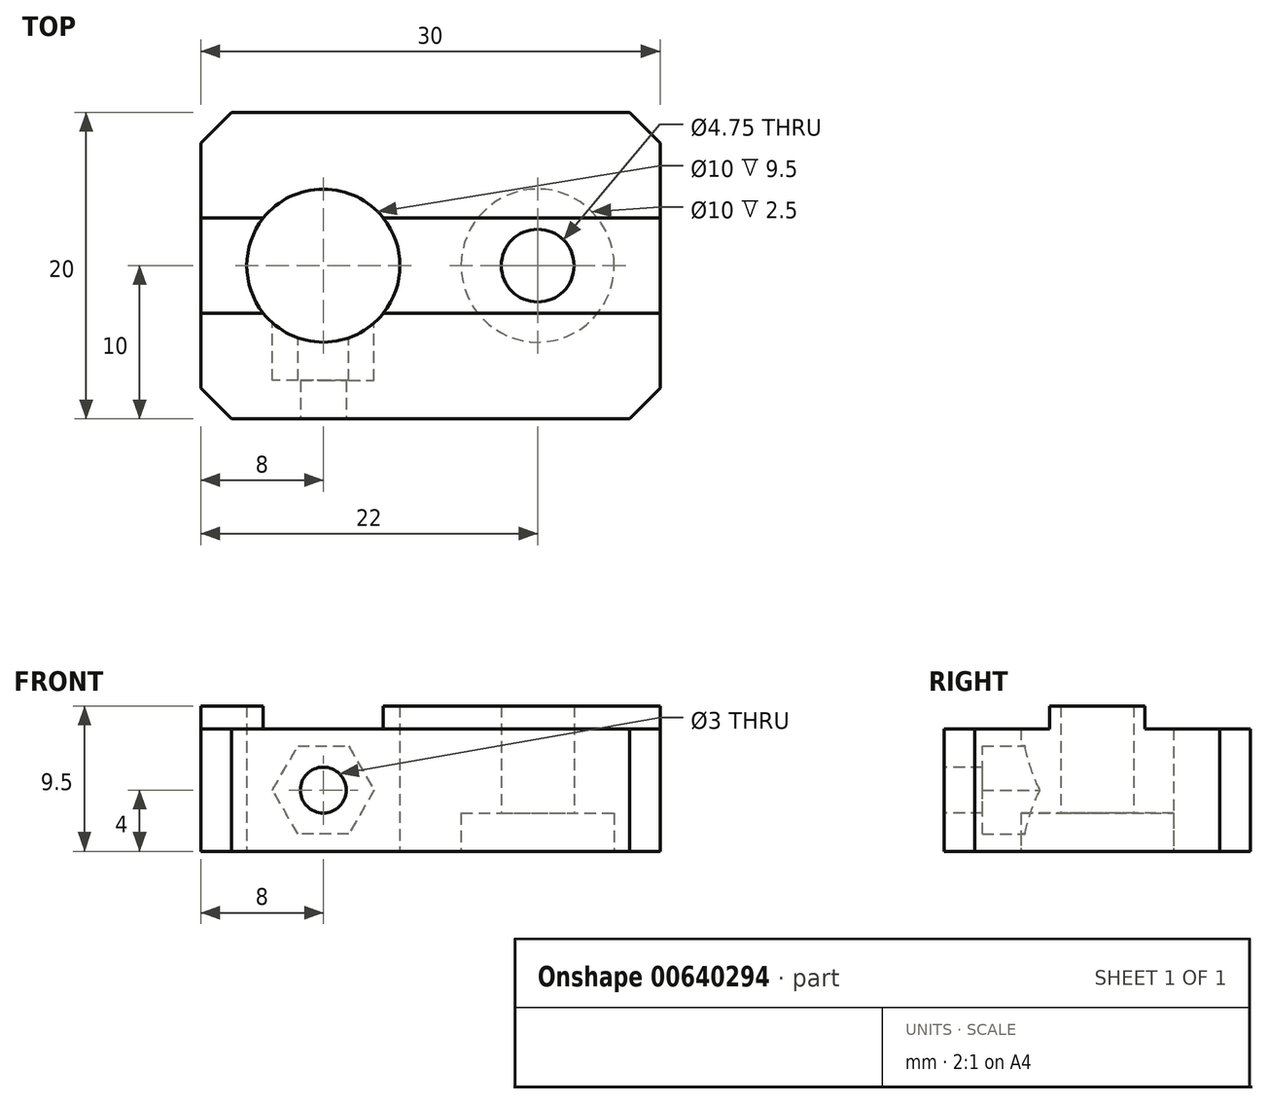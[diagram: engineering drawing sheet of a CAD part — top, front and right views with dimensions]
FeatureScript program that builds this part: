
annotation { "Feature Type Name" : "Feature", "Feature Type Description" : "" }
export const myFeature = defineFeature(function(context is Context, id is Id, definition is map)
    precondition{}
    {
        {
            var Q0;
            Q0=qCreatedBy(makeId("Top.planeOp"),FACE);
            var sketch = newSketch(context, id + "F0", { "sketchPlane" : qUnion([Q0])});
            skCircle(sketch, "E0", {"center": v(0, 0) * mm, "radius": 5 * mm});
            skLineSegment(sketch, "E1", {"start": v(0, 0) * mm, "end": v(0, 10) * mm, "construction": true});
            skLineSegment(sketch, "E2", {"start": v(0, 10) * mm, "end": v(-8, 10) * mm});
            skLineSegment(sketch, "E3", {"start": v(-8, 10) * mm, "end": v(-8, -10) * mm});
            skLineSegment(sketch, "E4", {"start": v(-8, -10) * mm, "end": v(22, -10) * mm});
            skLineSegment(sketch, "E5", {"start": v(22, -10) * mm, "end": v(22, 10) * mm});
            skLineSegment(sketch, "E6", {"start": v(22, 10) * mm, "end": v(0, 10) * mm});
            skLineSegment(sketch, "E7", {"start": v(22, 0) * mm, "end": v(14, 0) * mm, "construction": true});
            skPoint(sketch, "E7.endSnap0", {"position": v(22, 0) * mm});
            skCircle(sketch, "E8", {"center": v(14, 0) * mm, "radius": 2.38 * mm});
            skCircle(sketch, "E9", {"center": v(14, 0) * mm, "radius": 4.58 * mm, "construction": true});
            skSolve(sketch);
        }
        {
            var Q0;
            Q0=qSketchRegion(id+"F0",true);
            extrude(context, id + "F1", {"entities" : qUnion([Q0]), "depth" : 8 * mm, "offsetDistance" : 25 * mm});
        }
        {
            var Q0;
            Q0=makeQuery(id+"F1.opExtrude","CAP_FACE",FACE,{"disambiguationData":[OSD([sQuery(id+"F0.wireOp",EDGE,"E0"),sQuery(id+"F0.wireOp",EDGE,"E2"),sQuery(id+"F0.wireOp",EDGE,"E3"),sQuery(id+"F0.wireOp",EDGE,"E4"),sQuery(id+"F0.wireOp",EDGE,"E5"),sQuery(id+"F0.wireOp",EDGE,"E6"),sQuery(id+"F0.wireOp",EDGE,"E8")])],"isStart":false});
            var sketch = newSketch(context, id + "F2", { "sketchPlane" : qUnion([Q0])});
            skLineSegment(sketch, "E10", {"start": v(0, 0) * mm, "end": v(0, 3.1) * mm, "construction": true});
            skLineSegment(sketch, "E11", {"start": v(0, 0) * mm, "end": v(0, -3.1) * mm, "construction": true});
            skLineSegment(sketch, "E12", {"start": v(22, 3.1) * mm, "end": v(3.92, 3.1) * mm});
            skLineSegment(sketch, "E13", {"start": v(-8, 3.1) * mm, "end": v(-8, -3.1) * mm});
            skLineSegment(sketch, "E14", {"start": v(-8, -3.1) * mm, "end": v(-3.92, -3.1) * mm});
            skLineSegment(sketch, "E15", {"start": v(22, -3.1) * mm, "end": v(22, 3.1) * mm});
            skArc(sketch, "E16.0", {"start": v(3.92, -3.1) * mm, "mid": v(5, 0) * mm, "end": v(3.92, 3.1) * mm});
            skCircle(sketch, "E16.1", {"center": v(14, 0) * mm, "radius": 2.37 * mm});
            skLineSegment(sketch, "E17.trimOffspring", {"start": v(-3.92, 3.1) * mm, "end": v(-8, 3.1) * mm});
            skLineSegment(sketch, "E18.trimOffspring", {"start": v(3.92, -3.1) * mm, "end": v(22, -3.1) * mm});
            skArc(sketch, "E19.trimOffspring", {"start": v(-3.92, 3.1) * mm, "mid": v(-5, 0) * mm, "end": v(-3.92, -3.1) * mm});
            skSolve(sketch);
        }
        {
            var Q0;
            Q0=qSketchRegion(id+"F2",true);
            extrude(context, id + "F3", {"entities" : qUnion([Q0]), "operationType" : NewBodyOperationType.ADD, "depth" : 1.5 * mm, "offsetDistance" : 25 * mm});
        }
        {
            var Q0;
            Q0=makeQuery(id+"F1.opExtrude","SWEPT_FACE",FACE,{"disambiguationData":[OSD([sQuery(id+"F0.wireOp",EDGE,"E4")])]});
            var sketch = newSketch(context, id + "F4", { "sketchPlane" : qUnion([Q0])});
            skPoint(sketch, "E20.0", {"position": v(0, 0) * mm});
            skLineSegment(sketch, "E21", {"start": v(0, 0) * mm, "end": v(0, 8) * mm, "construction": true});
            skCircle(sketch, "E22", {"center": v(0, 4) * mm, "radius": 1.5 * mm});
            skSolve(sketch);
        }
        {
            var Q0;
            Q0=qSketchRegion(id+"F4",true);
            extrude(context, id + "F5", {"entities" : qUnion([Q0]), "operationType" : NewBodyOperationType.REMOVE, "oppositeDirection" : true, "depth" : 10 * mm, "offsetDistance" : 25 * mm});
        }
        {
            var Q0;
            Q0=qCreatedBy(makeId("Front.planeOp"),FACE);
            var sketch = newSketch(context, id + "F6", { "sketchPlane" : qUnion([Q0])});
            skCircle(sketch, "E23.0", {"center": v(0, 4) * mm, "radius": 1.5 * mm, "construction": true});
            skCircle(sketch, "E24.cCircle", {"center": v(0, 4) * mm, "radius": 2.88 * mm, "construction": true});
            skLineSegment(sketch, "E24.0", {"start": v(1.66, 1.13) * mm, "end": v(-1.66, 1.13) * mm});
            skLineSegment(sketch, "E24.1", {"start": v(-1.66, 1.12) * mm, "end": v(-3.32, 4) * mm});
            skLineSegment(sketch, "E24.2", {"start": v(-3.32, 4) * mm, "end": v(-1.66, 6.88) * mm});
            skLineSegment(sketch, "E24.3", {"start": v(-1.66, 6.87) * mm, "end": v(1.66, 6.87) * mm});
            skLineSegment(sketch, "E24.4", {"start": v(1.66, 6.88) * mm, "end": v(3.32, 4) * mm});
            skLineSegment(sketch, "E24.5", {"start": v(3.32, 4) * mm, "end": v(1.66, 1.12) * mm});
            skPoint(sketch, "E24.0.midPoint", {"position": v(0, 1.13) * mm});
            skSolve(sketch);
        }
        {
            var Q0;
            Q0=qSketchRegion(id+"F6",true);
            extrude(context, id + "F7", {"entities" : qUnion([Q0]), "operationType" : NewBodyOperationType.REMOVE, "depth" : 7.5 * mm, "offsetDistance" : 25 * mm});
        }
        {
            var Q0;
            Q0=makeQuery(id+"F1.opExtrude","SWEPT_EDGE",EDGE,{"disambiguationData":[OSD([sQuery(id+"F0.wireOp",EDGE,"E2"),sQuery(id+"F0.wireOp",EDGE,"E3")])]});
            var Q1;
            Q1=makeQuery(id+"F1.opExtrude","SWEPT_EDGE",EDGE,{"disambiguationData":[OSD([sQuery(id+"F0.wireOp",EDGE,"E5"),sQuery(id+"F0.wireOp",EDGE,"E6")])]});
            var Q2;
            Q2=makeQuery(id+"F1.opExtrude","SWEPT_EDGE",EDGE,{"disambiguationData":[OSD([sQuery(id+"F0.wireOp",EDGE,"E4"),sQuery(id+"F0.wireOp",EDGE,"E5")])]});
            var Q3;
            Q3=makeQuery(id+"F1.opExtrude","SWEPT_EDGE",EDGE,{"disambiguationData":[OSD([sQuery(id+"F0.wireOp",EDGE,"E3"),sQuery(id+"F0.wireOp",EDGE,"E4")])]});
            chamfer(context, id + "F8", {"entities" : qUnion([Q0, Q1, Q2, Q3]), "width" : 2 * mm, "tangentPropagation" : true});
        }
        {
            var Q0;
            Q0=makeQuery(id+"F1.opExtrude","CAP_FACE",FACE,{"disambiguationData":[OSD([sQuery(id+"F0.wireOp",EDGE,"E0"),sQuery(id+"F0.wireOp",EDGE,"E2"),sQuery(id+"F0.wireOp",EDGE,"E3"),sQuery(id+"F0.wireOp",EDGE,"E4"),sQuery(id+"F0.wireOp",EDGE,"E5"),sQuery(id+"F0.wireOp",EDGE,"E6"),sQuery(id+"F0.wireOp",EDGE,"E8")])],"isStart":true});
            var sketch = newSketch(context, id + "F9", { "sketchPlane" : qUnion([Q0])});
            skPoint(sketch, "E25.1", {"position": v(0, 0) * mm});
            skSolve(sketch);
        }
        {
            var Q0;
            {var subQ6=sQuery(id+"F0.wireOp",EDGE,"E0");Q0=makeQuery(id+"F9.imprint","IMPRINT",FACE,{"disambiguationData":[TD([[makeQuery(id+"F9.imprint","IMPRINT",EDGE,{"derivedFrom":makeQuery(id+"F1.opExtrude","CAP_EDGE",EDGE,{"disambiguationData":[OSD([subQ6])],"isStart":true})}),1.0]])]});}
            var sketch = newSketch(context, id + "F10", { "sketchPlane" : qUnion([Q0])});
            skCircle(sketch, "E26.0", {"center": v(14, 0) * mm, "radius": 2.37 * mm, "construction": true});
            skCircle(sketch, "E27", {"center": v(14, 0) * mm, "radius": 5 * mm});
            skSolve(sketch);
        }
        {
            var Q0;
            Q0 = qSketchRegion(id + "F10", true);
            extrude(context, id + "F11", {"entities" : qUnion([Q0]), "operationType" : NewBodyOperationType.REMOVE, "oppositeDirection" : true, "depth" : 2.5 * mm, "offsetDistance" : 25 * mm});
        }
    });
